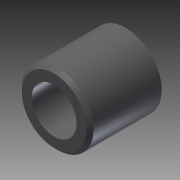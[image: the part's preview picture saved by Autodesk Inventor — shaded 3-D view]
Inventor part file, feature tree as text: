
AUTODESK INVENTOR PART (.ipt)
format: ipt  version: 2015 (Build 190159000, 159)  size: 90,624 bytes
history: native  units: mm
features: revolve x1, chamfer x1
ambient origin geometry x8: Origin, YZ Plane, XZ Plane, XY Plane, X Axis, Y Axis, Z Axis, Center Point
bodies: Solid1 (feature_tree)
feature tree (2):
  revolve  "Revolución1"  [1 undecoded]
  chamfer  "Chaflán1"  Distance=2.5mm
note: 1 required parameter value undecoded (feature->parameter linkage not recoverable at this tier; creation-order binding heuristic only, values carry confidence <= 0.55)
